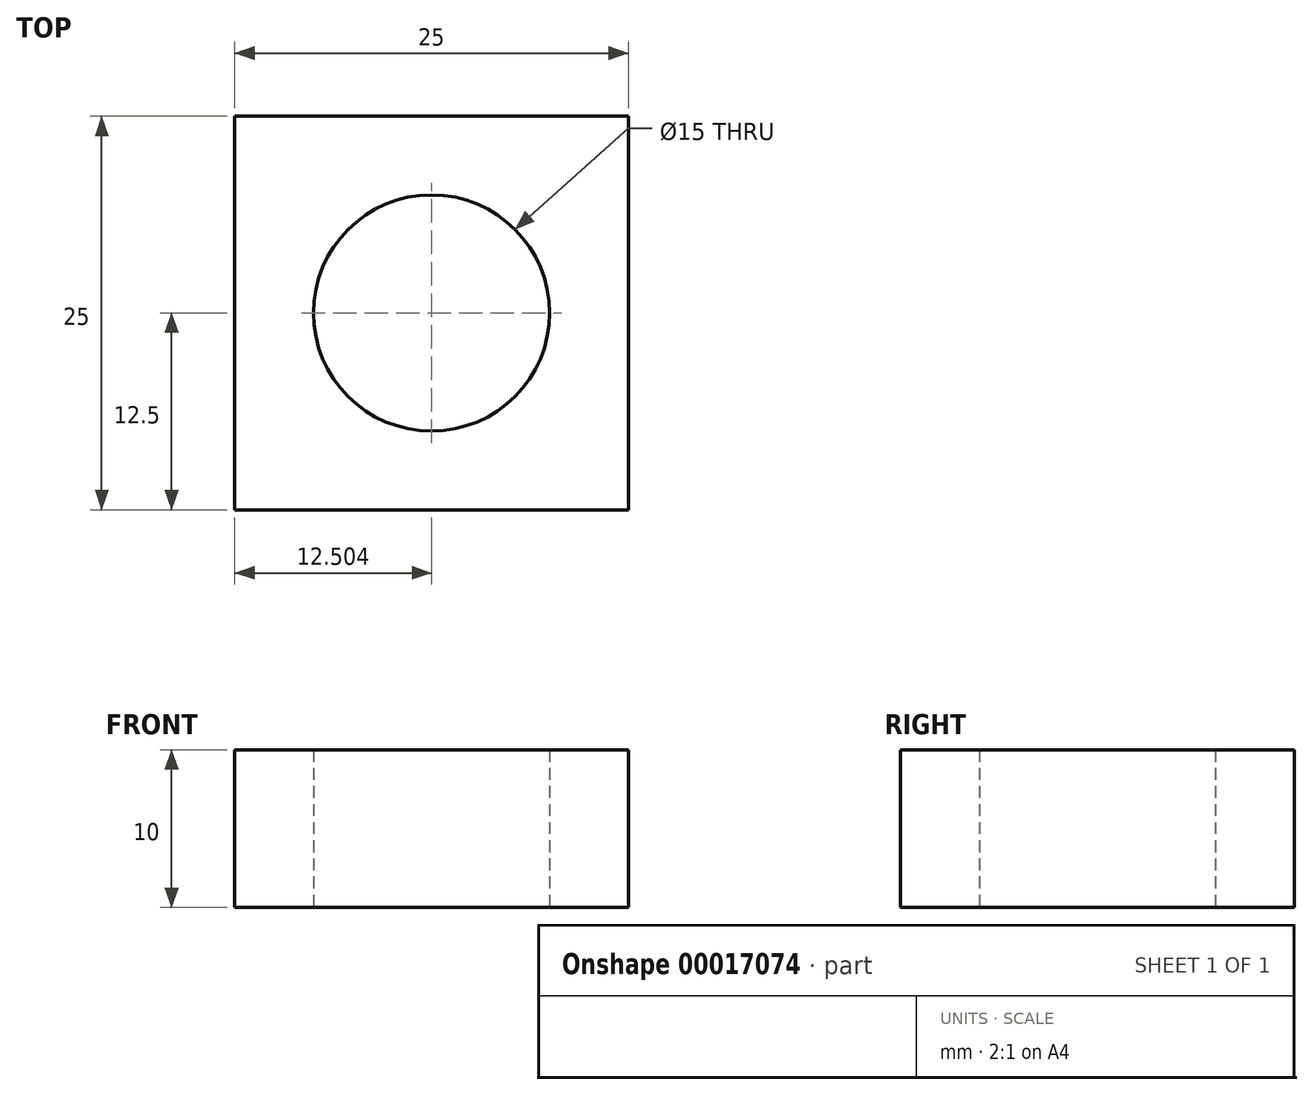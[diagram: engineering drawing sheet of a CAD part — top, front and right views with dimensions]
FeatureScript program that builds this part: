
annotation { "Feature Type Name" : "Feature", "Feature Type Description" : "" }
export const myFeature = defineFeature(function(context is Context, id is Id, definition is map)
    precondition{}
    {
        {
            var Q0;
            Q0=qCreatedBy(makeId("Top.planeOp"),FACE);
            var sketch = newSketch(context, id + "F0", { "sketchPlane" : qUnion([Q0])});
            skLineSegment(sketch, "E0.bottom", {"start": v(-30.94, -8.18) * mm, "end": v(-5.94, -8.18) * mm});
            skLineSegment(sketch, "E0.top", {"start": v(-30.94, -33.18) * mm, "end": v(-5.94, -33.18) * mm});
            skLineSegment(sketch, "E0.left", {"start": v(-30.94, -8.18) * mm, "end": v(-30.94, -33.18) * mm});
            skLineSegment(sketch, "E0.right", {"start": v(-5.94, -8.18) * mm, "end": v(-5.94, -33.18) * mm});
            skLineSegment(sketch, "E1", {"start": v(-30.94, -33.18) * mm, "end": v(-5.94, -8.18) * mm});
            skLineSegment(sketch, "E2", {"start": v(-5.94, -33.18) * mm, "end": v(-30.94, -8.18) * mm});
            skCircle(sketch, "E3", {"center": v(-18.44, -20.68) * mm, "radius": 7.5 * mm});
            skSolve(sketch);
        }
        {
            var Q0;
            {var subQ5=sQuery(id+"F0.wireOp",EDGE,"E0.bottom");Q0=makeQuery(id+"F0.imprint","IMPRINT",FACE,{"disambiguationData":[TD([[makeQuery(id+"F0.imprint","IMPRINT",EDGE,{"derivedFrom":subQ5}),-1.0]])]});}
            var Q1;
            {var subQ5=sQuery(id+"F0.wireOp",EDGE,"E0.top");Q1=makeQuery(id+"F0.imprint","IMPRINT",FACE,{"disambiguationData":[TD([[makeQuery(id+"F0.imprint","IMPRINT",EDGE,{"derivedFrom":subQ5}),1.0]])]});}
            var Q2;
            {var subQ5=sQuery(id+"F0.wireOp",EDGE,"E0.left");Q2=makeQuery(id+"F0.imprint","IMPRINT",FACE,{"disambiguationData":[TD([[makeQuery(id+"F0.imprint","IMPRINT",EDGE,{"derivedFrom":subQ5}),1.0]])]});}
            var Q3;
            {var subQ5=sQuery(id+"F0.wireOp",EDGE,"E0.right");Q3=makeQuery(id+"F0.imprint","IMPRINT",FACE,{"disambiguationData":[TD([[makeQuery(id+"F0.imprint","IMPRINT",EDGE,{"derivedFrom":subQ5}),-1.0]])]});}
            extrude(context, id + "F1", {"entities" : qUnion([Q0, Q1, Q2, Q3]), "depth" : 10 * mm});
        }
    });
